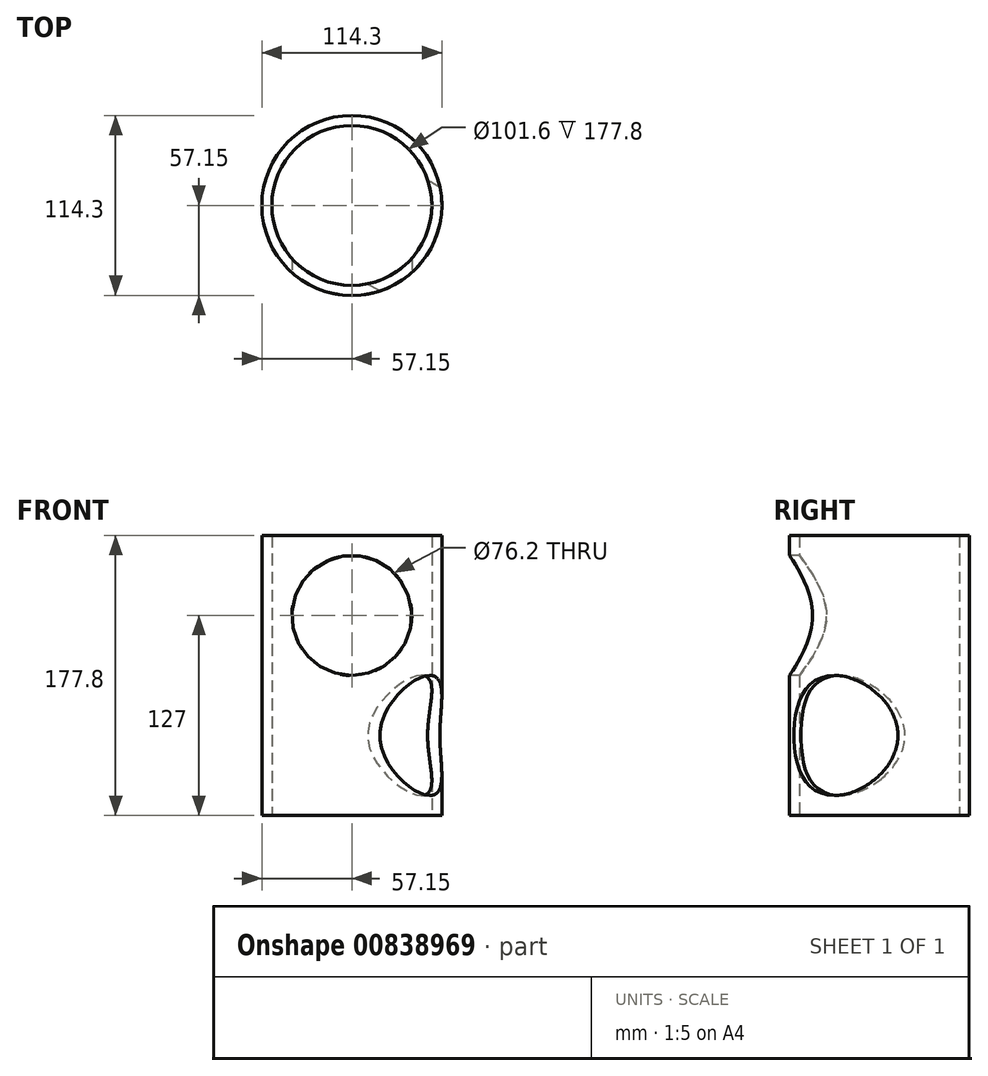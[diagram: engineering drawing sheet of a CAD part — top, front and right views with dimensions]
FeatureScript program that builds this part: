
annotation { "Feature Type Name" : "Feature", "Feature Type Description" : "" }
export const myFeature = defineFeature(function(context is Context, id is Id, definition is map)
    precondition{}
    {
        {
            var Q0;
            Q0=qCreatedBy(makeId("Front.planeOp"),FACE);
            var sketch = newSketch(context, id + "F0", { "sketchPlane" : qUnion([Q0])});
            skLineSegment(sketch, "E0", {"start": v(0, 0) * mm, "end": v(0, 213.19) * mm, "construction": true});
            skSolve(sketch);
        }
        {
            var Q0;
            Q0=qCreatedBy(makeId("Top.planeOp"),FACE);
            var sketch = newSketch(context, id + "F1", { "sketchPlane" : qUnion([Q0])});
            skCircle(sketch, "E1", {"center": v(0, 0) * mm, "radius": 50.8 * mm});
            skCircle(sketch, "E2", {"center": v(0, 0) * mm, "radius": 57.15 * mm});
            skSolve(sketch);
        }
        {
            var Q0;
            Q0=makeQuery(id+"F1.imprint","IMPRINT",FACE,{"disambiguationData":[TD([[makeQuery(id+"F1.imprint","IMPRINT",EDGE,{"derivedFrom":sQuery(id+"F1.wireOp",EDGE,"E1")}),-1.0]])]});
            extrude(context, id + "F2", {"entities" : qUnion([Q0]), "depth" : 177.8 * mm, "offsetDistance" : 25.4 * mm});
        }
        {
            var Q0;
            Q0=qCreatedBy(makeId("Top.planeOp"),FACE);
            var sketch = newSketch(context, id + "F3", { "sketchPlane" : qUnion([Q0])});
            skCircle(sketch, "E3.cCircle", {"center": v(0, 0) * mm, "radius": 57.15 * mm, "construction": true});
            skLineSegment(sketch, "E3.0", {"start": v(57.15, 15.31) * mm, "end": v(57.15, -15.31) * mm});
            skLineSegment(sketch, "E3.1", {"start": v(57.15, -15.31) * mm, "end": v(41.84, -41.84) * mm});
            skLineSegment(sketch, "E3.2", {"start": v(41.84, -41.84) * mm, "end": v(15.31, -57.15) * mm});
            skLineSegment(sketch, "E3.3", {"start": v(15.31, -57.15) * mm, "end": v(-15.31, -57.15) * mm});
            skLineSegment(sketch, "E3.4", {"start": v(-15.31, -57.15) * mm, "end": v(-41.84, -41.84) * mm});
            skLineSegment(sketch, "E3.5", {"start": v(-41.84, -41.84) * mm, "end": v(-57.15, -15.31) * mm});
            skLineSegment(sketch, "E3.6", {"start": v(-57.15, -15.31) * mm, "end": v(-57.15, 15.31) * mm});
            skLineSegment(sketch, "E3.7", {"start": v(-57.15, 15.31) * mm, "end": v(-41.84, 41.84) * mm});
            skLineSegment(sketch, "E3.8", {"start": v(-41.84, 41.84) * mm, "end": v(-15.31, 57.15) * mm});
            skLineSegment(sketch, "E3.9", {"start": v(-15.31, 57.15) * mm, "end": v(15.31, 57.15) * mm});
            skLineSegment(sketch, "E3.10", {"start": v(15.31, 57.15) * mm, "end": v(41.84, 41.84) * mm});
            skLineSegment(sketch, "E3.11", {"start": v(41.84, 41.84) * mm, "end": v(57.15, 15.31) * mm});
            skPoint(sketch, "E3.0.midPoint", {"position": v(57.15, 0) * mm});
            skSolve(sketch);
        }
        {
            var Q0;
            Q0=sQuery(id+"F3.wireOp",EDGE,"E3.1");
            cPlane(context, id + "F4", {"entities" : qUnion([Q0]), "cplaneType" : CPlaneType.LINE_ANGLE, "offset" : 25.4 * mm, "angle" : 90 * degree, "width" : 152.4 * mm, "height" : 152.4 * mm});
        }
        {
            var Q0;
            Q0=sQuery(id+"F3.wireOp",EDGE,"E3.3");
            cPlane(context, id + "F5", {"entities" : qUnion([Q0]), "cplaneType" : CPlaneType.LINE_ANGLE, "offset" : 25.4 * mm, "angle" : 0 * degree, "width" : 152.4 * mm, "height" : 152.4 * mm});
        }
        {
            var Q0;
            Q0=qCreatedBy(id+"F4.planeOp",FACE);
            var sketch = newSketch(context, id + "F6", { "sketchPlane" : qUnion([Q0])});
            skCircle(sketch, "E4", {"center": v(0, 50.8) * mm, "radius": 38.1 * mm});
            skSolve(sketch);
        }
        {
            var Q0;
            Q0=makeQuery(id+"F6.imprint","IMPRINT",FACE,{"disambiguationData":[TD([[makeQuery(id+"F6.imprint","IMPRINT",EDGE,{"derivedFrom":sQuery(id+"F6.wireOp",EDGE,"E4")}),1.0]])]});
            var Q1;
            Q1=makeQuery(id+"F2.opExtrude","SWEPT_FACE",FACE,{"disambiguationData":[OSD([sQuery(id+"F1.wireOp",EDGE,"E1")])]});
            extrude(context, id + "F7", {"entities" : qUnion([Q0]), "operationType" : NewBodyOperationType.REMOVE, "endBound" : BoundingType.UP_TO_SURFACE, "oppositeDirection" : true, "depth" : 25.4 * mm, "endBoundEntityFace" : qUnion([Q1]), "offsetDistance" : 25.4 * mm});
        }
        {
            var Q0;
            Q0=qCreatedBy(id+"F5.planeOp",FACE);
            var sketch = newSketch(context, id + "F8", { "sketchPlane" : qUnion([Q0])});
            skCircle(sketch, "E5", {"center": v(0, 127) * mm, "radius": 38.1 * mm});
            skSolve(sketch);
        }
        {
            var Q0;
            Q0=makeQuery(id+"F8.imprint","IMPRINT",FACE,{"disambiguationData":[TD([[makeQuery(id+"F8.imprint","IMPRINT",EDGE,{"derivedFrom":sQuery(id+"F8.wireOp",EDGE,"E5")}),1.0]])]});
            var Q1;
            Q1=makeQuery(id+"F2.opExtrude","SWEPT_FACE",FACE,{"disambiguationData":[OSD([sQuery(id+"F1.wireOp",EDGE,"E1")])]});
            extrude(context, id + "F9", {"entities" : qUnion([Q0]), "operationType" : NewBodyOperationType.REMOVE, "endBound" : BoundingType.UP_TO_SURFACE, "oppositeDirection" : true, "depth" : 25.4 * mm, "endBoundEntityFace" : qUnion([Q1]), "offsetDistance" : 25.4 * mm});
        }
    });
